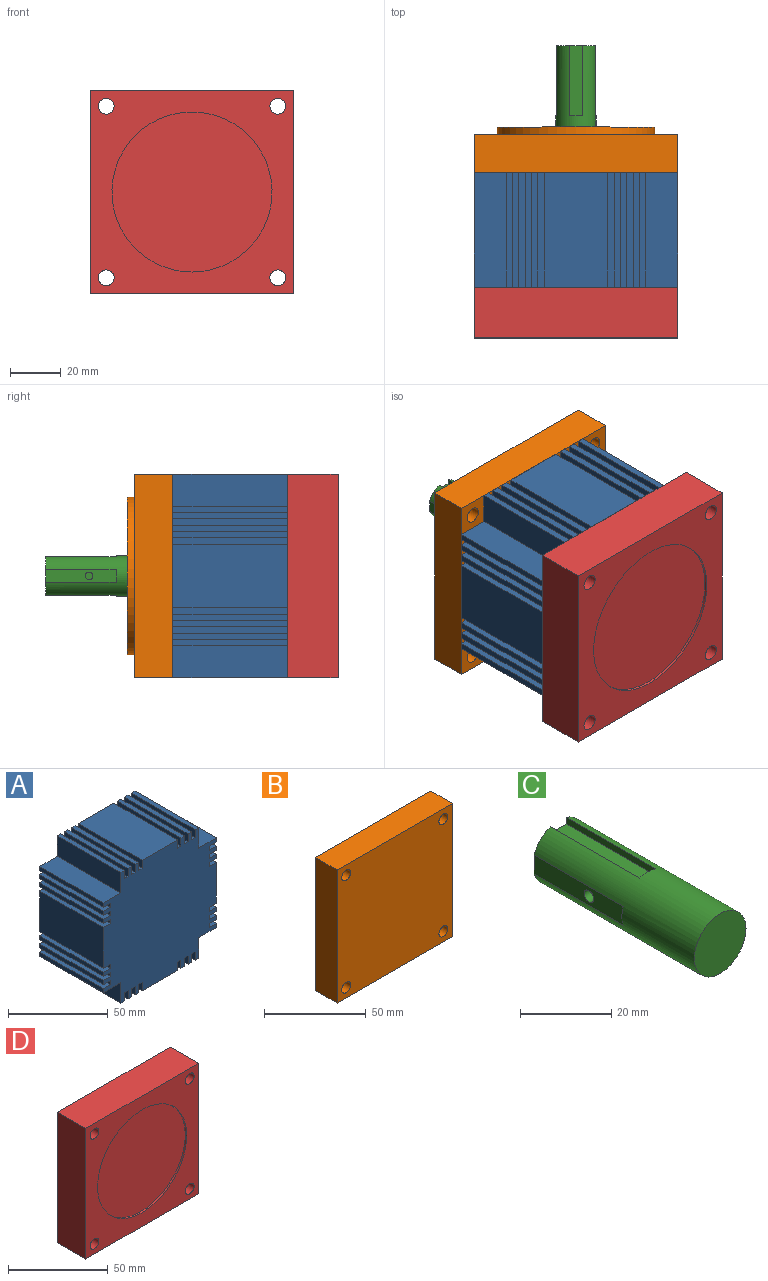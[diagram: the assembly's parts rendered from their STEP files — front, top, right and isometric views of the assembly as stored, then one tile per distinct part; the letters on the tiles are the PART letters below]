
ASSEMBLY  parts=4 mates=3
PART A: 110 faces, bbox 80x45x80 mm
  f0: plane 80x80mm, normal (0,-1,0), area 5475mm2, adj f2,f3,f4,f5,f6,f7,f8,f9
  f1: plane 80x80mm, normal (0,1,0), area 5475mm2, adj f2,f3,f4,f5,f6,f7,f8,f9
  f2: plane 45x2.5mm, normal (0,0,1), area 112.5mm2, adj f0,f1,f4,f109
  f3: plane 45x2.5mm, normal (1,0,0), area 112.5mm2, adj f0,f1,f107,f108
  f4: plane 45x5mm, normal (-1,0,0), area 225mm2, adj f0,f1,f2,f5
  f5: plane 45x2.5mm, normal (0,0,1), area 112.5mm2, adj f0,f1,f4,f6
  f6: plane 45x5mm, normal (1,0,0), area 225mm2, adj f0,f1,f5,f7
  f7: plane 45x2.5mm, normal (0,0,1), area 112.5mm2, adj f0,f1,f6,f8
  f8: plane 45x5mm, normal (-1,0,0), area 225mm2, adj f0,f1,f7,f9
  f9: plane 45x2.5mm, normal (0,0,1), area 112.5mm2, adj f0,f1,f8,f10
  f10: plane 45x5mm, normal (1,0,0), area 225mm2, adj f0,f1,f9,f11
  f11: plane 45x2.5mm, normal (0,0,1), area 112.5mm2, adj f0,f1,f10,f12
  f12: plane 45x5mm, normal (-1,0,0), area 225mm2, adj f0,f1,f11,f13
  f13: plane 45x2.5mm, normal (0,0,1), area 112.5mm2, adj f0,f1,f12,f14
  f14: plane 45x5mm, normal (1,0,0), area 225mm2, adj f0,f1,f13,f15
  f15: plane 45x25mm, normal (0,0,1), area 1125mm2, adj f0,f1,f14,f16
  f16: plane 45x5mm, normal (-1,0,0), area 225mm2, adj f0,f1,f15,f17
  f17: plane 45x2.5mm, normal (0,0,1), area 112.5mm2, adj f0,f1,f16,f18
  f18: plane 45x5mm, normal (1,0,0), area 225mm2, adj f0,f1,f17,f19
  f19: plane 45x2.5mm, normal (0,0,1), area 112.5mm2, adj f0,f1,f18,f20
  f20: plane 45x5mm, normal (-1,0,0), area 225mm2, adj f0,f1,f19,f21
  f21: plane 45x2.5mm, normal (0,0,1), area 112.5mm2, adj f0,f1,f20,f22
  f22: plane 45x5mm, normal (1,0,0), area 225mm2, adj f0,f1,f21,f23
  f23: plane 45x2.5mm, normal (0,0,1), area 112.5mm2, adj f0,f1,f22,f24
  f24: plane 45x5mm, normal (-1,0,0), area 225mm2, adj f0,f1,f23,f25
  f25: plane 45x2.5mm, normal (0,0,1), area 112.5mm2, adj f0,f1,f24,f26
  f26: plane 45x5mm, normal (1,0,0), area 225mm2, adj f0,f1,f25,f27
  f27: plane 45x2.5mm, normal (0,0,1), area 112.5mm2, adj f0,f1,f26,f28
  f28: plane 45x12.5mm, normal (-1,0,0), area 562.5mm2, adj f0,f1,f27,f29
  f29: plane 45x12.5mm, normal (0,0,1), area 562.5mm2, adj f0,f1,f28,f30
  f30: plane 45x2.5mm, normal (-1,0,0), area 112.5mm2, adj f0,f1,f29,f31
  f31: plane 45x5mm, normal (0,0,-1), area 225mm2, adj f0,f1,f30,f32
  f32: plane 45x2.5mm, normal (-1,0,0), area 112.5mm2, adj f0,f1,f31,f33
  f33: plane 45x5mm, normal (0,0,1), area 225mm2, adj f0,f1,f32,f34
  f34: plane 45x2.5mm, normal (-1,0,0), area 112.5mm2, adj f0,f1,f33,f35
  f35: plane 45x5mm, normal (0,0,-1), area 225mm2, adj f0,f1,f34,f36
  f36: plane 45x2.5mm, normal (-1,0,0), area 112.5mm2, adj f0,f1,f35,f37
  f37: plane 45x5mm, normal (0,0,1), area 225mm2, adj f0,f1,f36,f38
  f38: plane 45x2.5mm, normal (-1,0,0), area 112.5mm2, adj f0,f1,f37,f39
  f39: plane 45x5mm, normal (0,0,-1), area 225mm2, adj f0,f1,f38,f40
  f40: plane 45x2.5mm, normal (-1,0,0), area 112.5mm2, adj f0,f1,f39,f41
  f41: plane 45x5mm, normal (0,0,1), area 225mm2, adj f0,f1,f40,f42
  f42: plane 45x25mm, normal (-1,0,0), area 1125mm2, adj f0,f1,f41,f43
  f43: plane 45x5mm, normal (0,0,-1), area 225mm2, adj f0,f1,f42,f44
  f44: plane 45x2.5mm, normal (-1,0,0), area 112.5mm2, adj f0,f1,f43,f45
  f45: plane 45x5mm, normal (0,0,1), area 225mm2, adj f0,f1,f44,f46
  f46: plane 45x2.5mm, normal (-1,0,0), area 112.5mm2, adj f0,f1,f45,f47
  f47: plane 45x5mm, normal (0,0,-1), area 225mm2, adj f0,f1,f46,f48
  f48: plane 45x2.5mm, normal (-1,0,0), area 112.5mm2, adj f0,f1,f47,f49
  f49: plane 45x5mm, normal (0,0,1), area 225mm2, adj f0,f1,f48,f50
  f50: plane 45x2.5mm, normal (-1,0,0), area 112.5mm2, adj f0,f1,f49,f51
  f51: plane 45x5mm, normal (0,0,-1), area 225mm2, adj f0,f1,f50,f52
  f52: plane 45x2.5mm, normal (-1,0,0), area 112.5mm2, adj f0,f1,f51,f53
  f53: plane 45x5mm, normal (0,0,1), area 225mm2, adj f0,f1,f52,f54
  f54: plane 45x2.5mm, normal (-1,0,0), area 112.5mm2, adj f0,f1,f53,f55
  f55: plane 45x12.5mm, normal (0,0,-1), area 562.5mm2, adj f0,f1,f54,f56
  f56: plane 45x12.5mm, normal (-1,0,0), area 562.5mm2, adj f0,f1,f55,f57
  f57: plane 45x2.5mm, normal (0,0,-1), area 112.5mm2, adj f0,f1,f56,f58
  f58: plane 45x5mm, normal (1,0,0), area 225mm2, adj f0,f1,f57,f59
  f59: plane 45x2.5mm, normal (0,0,-1), area 112.5mm2, adj f0,f1,f58,f60
  f60: plane 45x5mm, normal (-1,0,0), area 225mm2, adj f0,f1,f59,f61
  f61: plane 45x2.5mm, normal (0,0,-1), area 112.5mm2, adj f0,f1,f60,f62
  f62: plane 45x5mm, normal (1,0,0), area 225mm2, adj f0,f1,f61,f63
  f63: plane 45x2.5mm, normal (0,0,-1), area 112.5mm2, adj f0,f1,f62,f64
  f64: plane 45x5mm, normal (-1,0,0), area 225mm2, adj f0,f1,f63,f65
  f65: plane 45x2.5mm, normal (0,0,-1), area 112.5mm2, adj f0,f1,f64,f66
  f66: plane 45x5mm, normal (1,0,0), area 225mm2, adj f0,f1,f65,f67
  f67: plane 45x2.5mm, normal (0,0,-1), area 112.5mm2, adj f0,f1,f66,f68
  f68: plane 45x5mm, normal (-1,0,0), area 225mm2, adj f0,f1,f67,f69
  f69: plane 45x25mm, normal (0,0,-1), area 1125mm2, adj f0,f1,f68,f70
  f70: plane 45x5mm, normal (1,0,0), area 225mm2, adj f0,f1,f69,f71
  f71: plane 45x2.5mm, normal (0,0,-1), area 112.5mm2, adj f0,f1,f70,f72
  f72: plane 45x5mm, normal (-1,0,0), area 225mm2, adj f0,f1,f71,f73
  f73: plane 45x2.5mm, normal (0,0,-1), area 112.5mm2, adj f0,f1,f72,f74
  f74: plane 45x5mm, normal (1,0,0), area 225mm2, adj f0,f1,f73,f75
  f75: plane 45x2.5mm, normal (0,0,-1), area 112.5mm2, adj f0,f1,f74,f76
  f76: plane 45x5mm, normal (-1,0,0), area 225mm2, adj f0,f1,f75,f77
  f77: plane 45x2.5mm, normal (0,0,-1), area 112.5mm2, adj f0,f1,f76,f78
  f78: plane 45x5mm, normal (1,0,0), area 225mm2, adj f0,f1,f77,f79
  f79: plane 45x2.5mm, normal (0,0,-1), area 112.5mm2, adj f0,f1,f78,f80
  f80: plane 45x5mm, normal (-1,0,0), area 225mm2, adj f0,f1,f79,f81
  f81: plane 45x2.5mm, normal (0,0,-1), area 112.5mm2, adj f0,f1,f80,f82
  f82: plane 45x12.5mm, normal (1,0,0), area 562.5mm2, adj f0,f1,f81,f83
  f83: plane 45x12.5mm, normal (0,0,-1), area 562.5mm2, adj f0,f1,f82,f84
  f84: plane 45x2.5mm, normal (1,0,0), area 112.5mm2, adj f0,f1,f83,f85
  f85: plane 45x5mm, normal (0,0,1), area 225mm2, adj f0,f1,f84,f86
  f86: plane 45x2.5mm, normal (1,0,0), area 112.5mm2, adj f0,f1,f85,f87
  f87: plane 45x5mm, normal (0,0,-1), area 225mm2, adj f0,f1,f86,f88
  f88: plane 45x2.5mm, normal (1,0,0), area 112.5mm2, adj f0,f1,f87,f89
  f89: plane 45x5mm, normal (0,0,1), area 225mm2, adj f0,f1,f88,f90
  f90: plane 45x2.5mm, normal (1,0,0), area 112.5mm2, adj f0,f1,f89,f91
  f91: plane 45x5mm, normal (0,0,-1), area 225mm2, adj f0,f1,f90,f92
  f92: plane 45x2.5mm, normal (1,0,0), area 112.5mm2, adj f0,f1,f91,f93
  f93: plane 45x5mm, normal (0,0,1), area 225mm2, adj f0,f1,f92,f94
  f94: plane 45x2.5mm, normal (1,0,0), area 112.5mm2, adj f0,f1,f93,f95
  f95: plane 45x5mm, normal (0,0,-1), area 225mm2, adj f0,f1,f94,f96
  f96: plane 45x25mm, normal (1,0,0), area 1125mm2, adj f0,f1,f95,f97
  f97: plane 45x5mm, normal (0,0,1), area 225mm2, adj f0,f1,f96,f98
  f98: plane 45x2.5mm, normal (1,0,0), area 112.5mm2, adj f0,f1,f97,f99
  f99: plane 45x5mm, normal (0,0,-1), area 225mm2, adj f0,f1,f98,f100
  f100: plane 45x2.5mm, normal (1,0,0), area 112.5mm2, adj f0,f1,f99,f101
  f101: plane 45x5mm, normal (0,0,1), area 225mm2, adj f0,f1,f100,f102
  f102: plane 45x2.5mm, normal (1,0,0), area 112.5mm2, adj f0,f1,f101,f103
  f103: plane 45x5mm, normal (0,0,-1), area 225mm2, adj f0,f1,f102,f104
  f104: plane 45x2.5mm, normal (1,0,0), area 112.5mm2, adj f0,f1,f103,f105
  f105: plane 45x5mm, normal (0,0,1), area 225mm2, adj f0,f1,f104,f106
  f106: plane 45x2.5mm, normal (1,0,0), area 112.5mm2, adj f0,f1,f105,f107
  f107: plane 45x5mm, normal (0,0,-1), area 225mm2, adj f0,f1,f3,f106
  f108: plane 45x12.5mm, normal (0,0,1), area 562.5mm2, adj f0,f1,f3,f109
  f109: plane 45x12.5mm, normal (1,0,0), area 562.5mm2, adj f0,f1,f2,f108
PART B: 18 faces, bbox 80x18x80 mm
  f0: plane 80x15mm, normal (0,0,-1), area 1200mm2, adj f1,f3,f4,f5
  f1: plane 80x15mm, normal (1,0,0), area 1200mm2, adj f0,f2,f4,f5
  f2: plane 80x15mm, normal (0,0,1), area 1200mm2, adj f1,f3,f4,f5
  f3: plane 80x15mm, normal (-1,0,0), area 1200mm2, adj f0,f2,f4,f5
  f4: plane 80x80mm, normal (0,-1,0), area 6279.2mm2, adj f0,f1,f2,f3,f14,f15,f16,f17
  f5: plane 80x80mm, normal (0,1,0), area 3260.2mm2, adj f0,f1,f2,f3,f7,f14,f15,f16
  f6: cylinder r=26mm len=52mm, axis (0,-1,0), area 490.1mm2, adj f8,f9
  f7: cylinder r=31mm len=62mm, axis (0,-1,0), area 584.3mm2, adj f5,f8
  f8: plane 62x62mm, normal (0,1,0), area 895.4mm2, adj f6,f7
  f9: plane 52x52mm, normal (0,1,0), area 989.6mm2, adj f6,f11
  f10: cylinder r=8.5mm len=17mm, axis (0,-1,0), area 160.2mm2, adj f12,f13
  f11: cylinder r=19mm len=38mm, axis (0,-1,0), area 358.1mm2, adj f9,f12
  f12: plane 38x38mm, normal (0,1,0), area 907.1mm2, adj f10,f11
  f13: plane 17x17mm, normal (0,1,0), area 227mm2, adj f10
  f14: cylinder r=3.1mm len=15mm, axis (0,-1,0), area 292.2mm2, adj f4,f5
  f15: cylinder r=3.1mm len=15mm, axis (0,-1,0), area 292.2mm2, adj f4,f5
  f16: cylinder r=3.1mm len=15mm, axis (0,-1,0), area 292.2mm2, adj f4,f5
  f17: cylinder r=3.1mm len=15mm, axis (0,-1,0), area 292.2mm2, adj f4,f5
PART C: 20 faces, bbox 16x50x16 mm
  f0: plane 27.6x5mm, normal (0,0,1), area 138mm2, adj f1,f5,f7,f15
  f1: plane 27.6x1.75mm, normal (-1,0,0), area 48.3mm2, adj f0,f6,f7,f15
  f2: plane 27.6x5mm, normal (1,0,0), area 130.9mm2, adj f6,f7,f9,f18
  f3: plane 27.6x5mm, normal (0,0,-1), area 130.9mm2, adj f6,f7,f13,f17
  f4: plane 27.6x5mm, normal (-1,0,0), area 130.9mm2, adj f6,f7,f11,f16
  f5: plane 27.6x1.75mm, normal (1,0,0), area 48.3mm2, adj f0,f6,f7,f15
  f6: cylinder r=8mm len=50mm, axis (0,-1,0), area 1838mm2, adj f1,f2,f3,f4,f5,f7,f8,f15
  f7: plane 15.2x15.2mm, normal (0,1,0), area 186.9mm2, adj f0,f1,f2,f3,f4,f5,f6
  f8: plane 16x16mm, normal (0,-1,0), area 201.1mm2, adj f6,f19
  f9: cylinder r=1.5mm len=4mm, axis (1,0,0), area 37.7mm2, adj f2,f10
  f10: plane 3x3mm, normal (1,0,0), area 7.1mm2, adj f9
  f11: cylinder r=1.5mm len=4mm, axis (-1,0,0), area 37.7mm2, adj f4,f12
  f12: plane 3x3mm, normal (-1,0,0), area 7.1mm2, adj f11
  f13: cylinder r=1.5mm len=4mm, axis (0,0,-1), area 37.7mm2, adj f3,f14
  f14: plane 3x3mm, normal (0,0,-1), area 7.1mm2, adj f13
  f15: plane 5x2.15mm, normal (0,1,0), area 10.1mm2, adj f0,f1,f5,f6
  f16: plane 5x0.4mm, normal (0,1,0), area 1.3mm2, adj f4,f6
  f17: plane 5x0.4mm, normal (0,1,0), area 1.3mm2, adj f3,f6
  f18: plane 5x0.4mm, normal (0,1,0), area 1.3mm2, adj f2,f19
  f19: extruded ~22.4x5mm, area 113.9mm2, adj f6,f8,f18
PART D: 12 faces, bbox 80x20x80 mm
  f0: plane 80x20mm, normal (0,0,1), area 1600mm2, adj f1,f3,f4,f5
  f1: plane 80x20mm, normal (-1,0,0), area 1600mm2, adj f0,f2,f4,f5
  f2: plane 80x20mm, normal (0,0,-1), area 1600mm2, adj f1,f3,f4,f5
  f3: plane 80x20mm, normal (1,0,0), area 1600mm2, adj f0,f2,f4,f5
  f4: plane 80x80mm, normal (0,-1,0), area 3162mm2, adj f0,f1,f2,f3,f6,f8,f9,f10
  f5: plane 80x80mm, normal (0,1,0), area 6279.2mm2, adj f0,f1,f2,f3,f8,f9,f10,f11
  f6: cylinder r=31.5mm len=63mm, axis (0,-1,0), area 197.9mm2, adj f4,f7
  f7: plane 63x63mm, normal (0,-1,0), area 3117.2mm2, adj f6
  f8: cylinder r=3.1mm len=20mm, axis (0,-1,0), area 389.6mm2, adj f4,f5
  f9: cylinder r=3.1mm len=20mm, axis (0,-1,0), area 389.6mm2, adj f4,f5
  f10: cylinder r=3.1mm len=20mm, axis (0,-1,0), area 389.6mm2, adj f4,f5
  f11: cylinder r=3.1mm len=20mm, axis (0,-1,0), area 389.6mm2, adj f4,f5
PLACE A t=(-69.98,-71.25,-3.6)mm
PLACE B t=(-69.98,-71.25,-3.6)mm
PLACE C t=(-69.98,-71.25,-3.6)mm
PLACE D t=(-69.98,-71.25,-3.6)mm
MATE fastened A.f0 <-> D.f6  axis (0,-1,0) through (-69.98,-131.25,-3.6)mm
MATE fastened C.f6 <-> A.f1  axis (0,-1,0) through (-69.98,-86.25,-3.6)mm
MATE fastened B.f7 <-> A.f1  axis (0,-1,0) through (-69.98,-86.25,-3.6)mm
